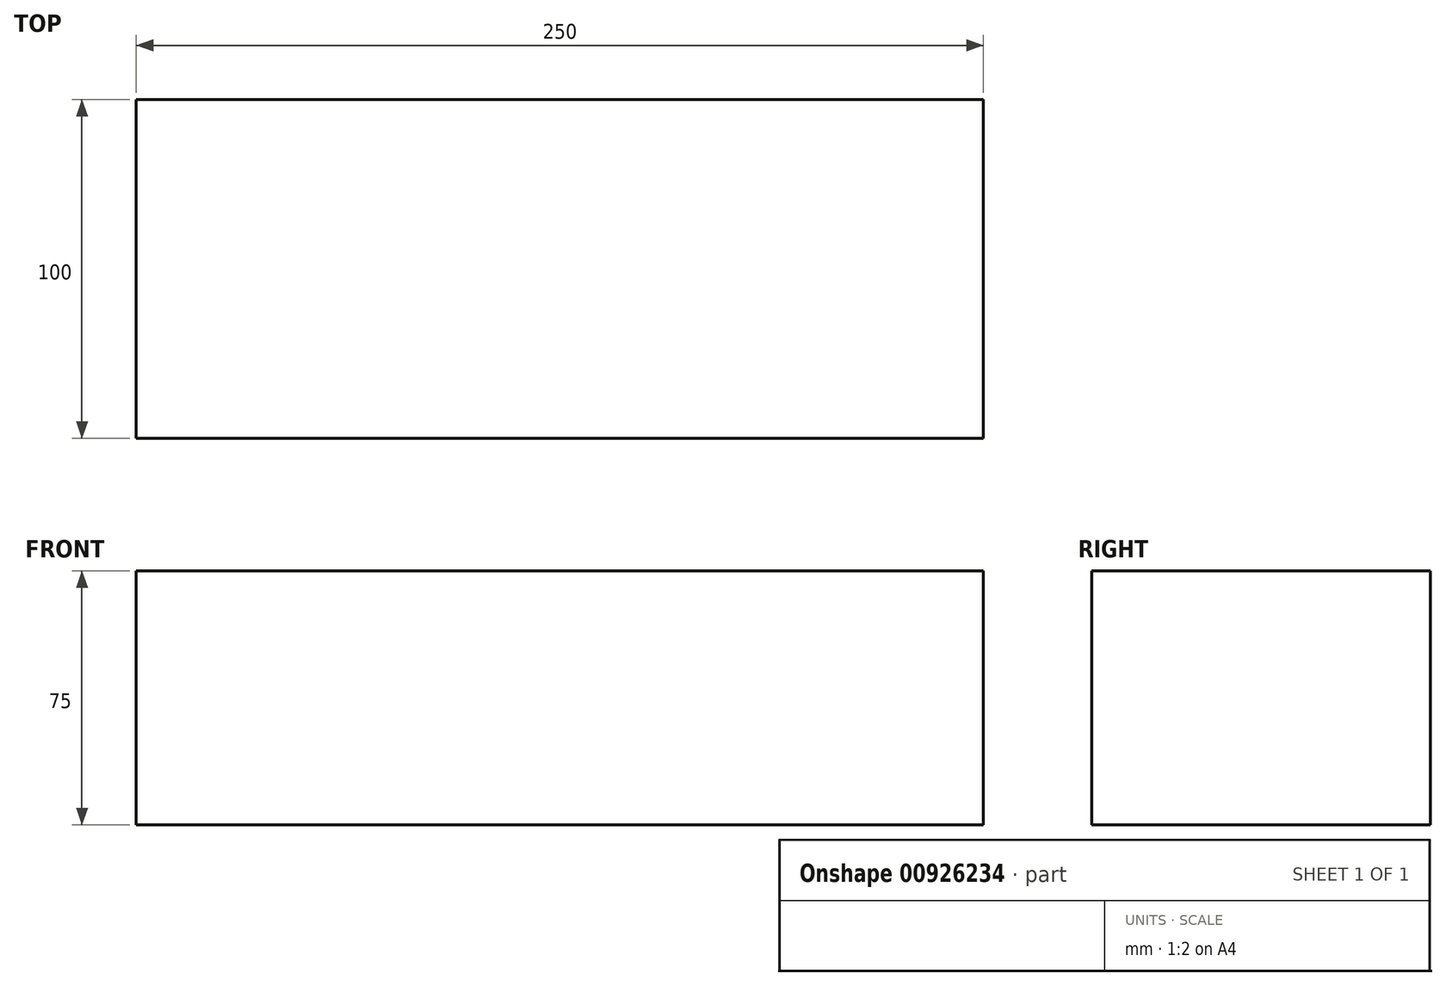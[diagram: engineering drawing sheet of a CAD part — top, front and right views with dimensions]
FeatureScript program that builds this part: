
annotation { "Feature Type Name" : "Feature", "Feature Type Description" : "" }
export const myFeature = defineFeature(function(context is Context, id is Id, definition is map)
    precondition{}
    {
        {
            var Q0;
            Q0=qCreatedBy(makeId("Top.planeOp"),FACE);
            var sketch = newSketch(context, id + "F0", { "sketchPlane" : qUnion([Q0])});
            skLineSegment(sketch, "E0.bottom", {"start": v(125, 50) * mm, "end": v(-125, 50) * mm});
            skLineSegment(sketch, "E0.top", {"start": v(125, -50) * mm, "end": v(-125, -50) * mm});
            skLineSegment(sketch, "E0.left", {"start": v(125, 50) * mm, "end": v(125, -50) * mm});
            skLineSegment(sketch, "E0.right", {"start": v(-125, 50) * mm, "end": v(-125, -50) * mm});
            skPoint(sketch, "E0.middle", {"position": v(0, 0) * mm});
            skSolve(sketch);
        }
        {
            var Q0;
            Q0=makeQuery(id+"F0.imprint","IMPRINT",FACE,{"disambiguationData":[TD([[makeQuery(id+"F0.imprint","IMPRINT",EDGE,{"derivedFrom":sQuery(id+"F0.wireOp",EDGE,"E0.bottom")}),1.0]])]});
            extrude(context, id + "F1", {"entities" : qUnion([Q0]), "depth" : 75 * mm, "offsetDistance" : 25 * mm});
        }
    });
